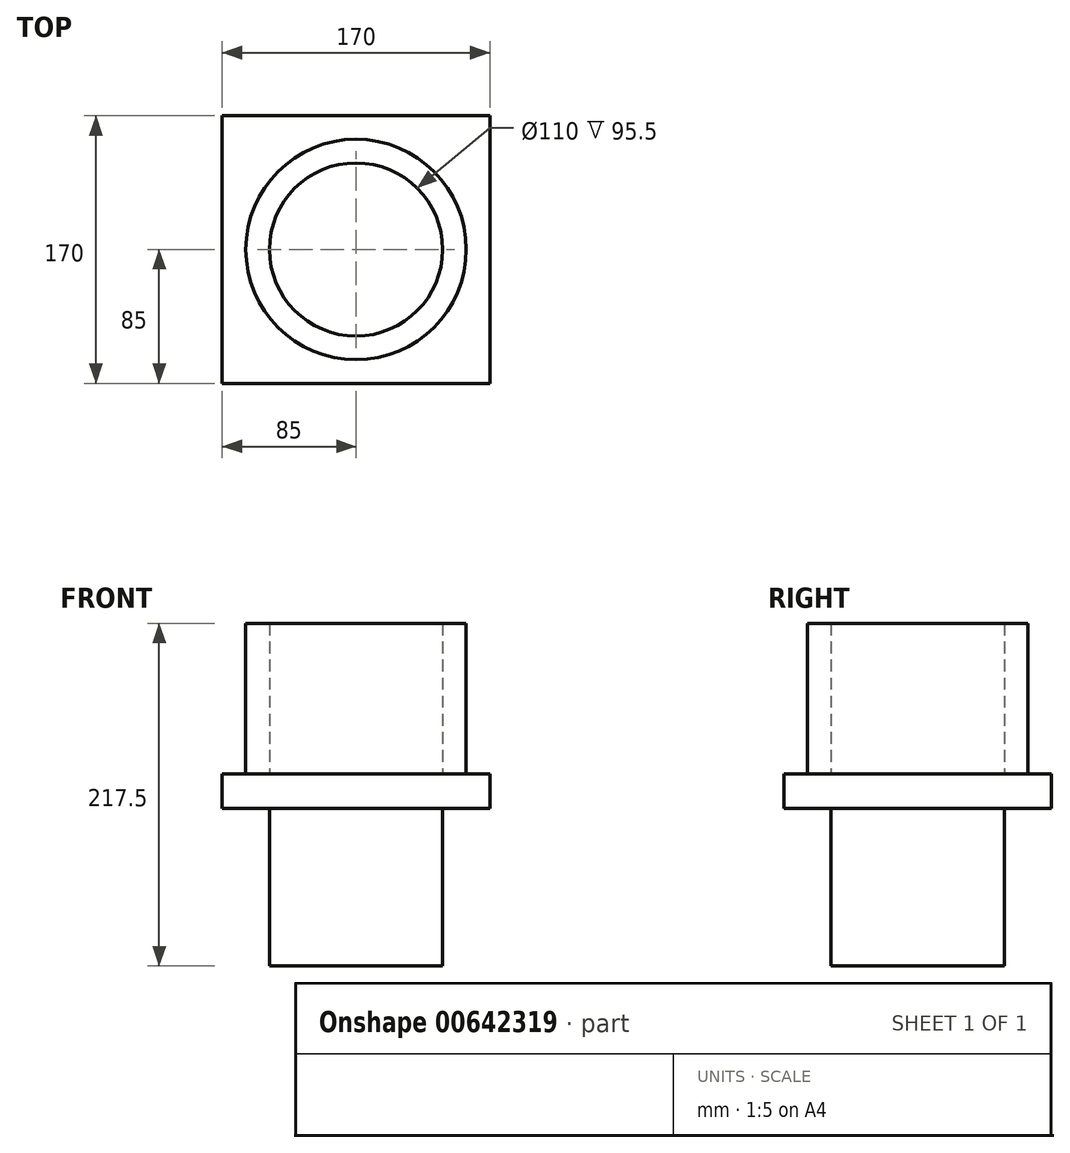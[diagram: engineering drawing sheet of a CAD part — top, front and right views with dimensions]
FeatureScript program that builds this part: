
annotation { "Feature Type Name" : "Feature", "Feature Type Description" : "" }
export const myFeature = defineFeature(function(context is Context, id is Id, definition is map)
    precondition{}
    {
        {
            var Q0;
            Q0=qCreatedBy(makeId("Top.planeOp"),FACE);
            var sketch = newSketch(context, id + "F0", { "sketchPlane" : qUnion([Q0])});
            skLineSegment(sketch, "E0.bottom", {"start": v(85, -85) * mm, "end": v(-85, -85) * mm});
            skLineSegment(sketch, "E0.top", {"start": v(85, 85) * mm, "end": v(-85, 85) * mm});
            skLineSegment(sketch, "E0.left", {"start": v(85, -85) * mm, "end": v(85, 85) * mm});
            skLineSegment(sketch, "E0.right", {"start": v(-85, -85) * mm, "end": v(-85, 85) * mm});
            skPoint(sketch, "E0.middle", {"position": v(0, 0) * mm});
            skSolve(sketch);
        }
        {
            var Q0;
            Q0=makeQuery(id+"F0.imprint","IMPRINT",FACE,{"disambiguationData":[TD([[makeQuery(id+"F0.imprint","IMPRINT",EDGE,{"derivedFrom":sQuery(id+"F0.wireOp",EDGE,"E0.bottom")}),-1.0]])]});
            extrude(context, id + "F1", {"entities" : qUnion([Q0]), "depth" : 17.5 * mm, "offsetDistance" : 25 * mm});
        }
        {
            var Q0;
            Q0=makeQuery(id+"F1.opExtrude","CAP_FACE",FACE,{"disambiguationData":[OSD([sQuery(id+"F0.wireOp",EDGE,"E0.bottom"),sQuery(id+"F0.wireOp",EDGE,"E0.top"),sQuery(id+"F0.wireOp",EDGE,"E0.left"),sQuery(id+"F0.wireOp",EDGE,"E0.right")])],"isStart":false});
            var sketch = newSketch(context, id + "F2", { "sketchPlane" : qUnion([Q0])});
            skCircle(sketch, "E1", {"center": v(0, 0) * mm, "radius": 70 * mm});
            skCircle(sketch, "E2", {"center": v(0, 0) * mm, "radius": 55 * mm});
            skSolve(sketch);
        }
        {
            var Q0;
            Q0=makeQuery(id+"F2.imprint","IMPRINT",FACE,{"disambiguationData":[TD([[makeQuery(id+"F2.imprint","IMPRINT",EDGE,{"derivedFrom":sQuery(id+"F2.wireOp",EDGE,"E1")}),1.0]])]});
            extrude(context, id + "F3", {"entities" : qUnion([Q0]), "operationType" : NewBodyOperationType.ADD, "depth" : 100 * mm, "offsetDistance" : 25 * mm});
        }
        {
            var Q0;
            Q0=qCreatedBy(makeId("Top.planeOp"),FACE);
            var sketch = newSketch(context, id + "F4", { "sketchPlane" : qUnion([Q0])});
            skLineSegment(sketch, "E3.bottom", {"start": v(85, -85) * mm, "end": v(-85, -85) * mm});
            skLineSegment(sketch, "E3.top", {"start": v(85, 85) * mm, "end": v(-85, 85) * mm});
            skLineSegment(sketch, "E3.left", {"start": v(85, -85) * mm, "end": v(85, 85) * mm});
            skLineSegment(sketch, "E3.right", {"start": v(-85, -85) * mm, "end": v(-85, 85) * mm});
            skPoint(sketch, "E3.middle", {"position": v(0, 0) * mm});
            skSolve(sketch);
        }
        {
            var Q0;
            Q0=makeQuery(id+"F4.imprint","IMPRINT",FACE,{"disambiguationData":[TD([[makeQuery(id+"F4.imprint","IMPRINT",EDGE,{"derivedFrom":sQuery(id+"F4.wireOp",EDGE,"E3.bottom")}),-1.0]])]});
            extrude(context, id + "F5", {"entities" : qUnion([Q0]), "depth" : 22 * mm, "offsetDistance" : 25 * mm});
        }
        {
            var Q0;
            Q0=makeQuery(id+"F5.opExtrude","CAP_FACE",FACE,{"disambiguationData":[OSD([sQuery(id+"F4.wireOp",EDGE,"E3.bottom"),sQuery(id+"F4.wireOp",EDGE,"E3.top"),sQuery(id+"F4.wireOp",EDGE,"E3.left"),sQuery(id+"F4.wireOp",EDGE,"E3.right")])],"isStart":true});
            var sketch = newSketch(context, id + "F6", { "sketchPlane" : qUnion([Q0])});
            skCircle(sketch, "E4", {"center": v(0, 0) * mm, "radius": 55 * mm});
            skSolve(sketch);
        }
        {
            var Q0;
            Q0=makeQuery(id+"F6.imprint","IMPRINT",FACE,{"disambiguationData":[TD([[makeQuery(id+"F6.imprint","IMPRINT",EDGE,{"derivedFrom":sQuery(id+"F6.wireOp",EDGE,"E4")}),1.0]])]});
            extrude(context, id + "F7", {"entities" : qUnion([Q0]), "operationType" : NewBodyOperationType.ADD, "depth" : 100 * mm, "offsetDistance" : 25 * mm});
        }
    });
